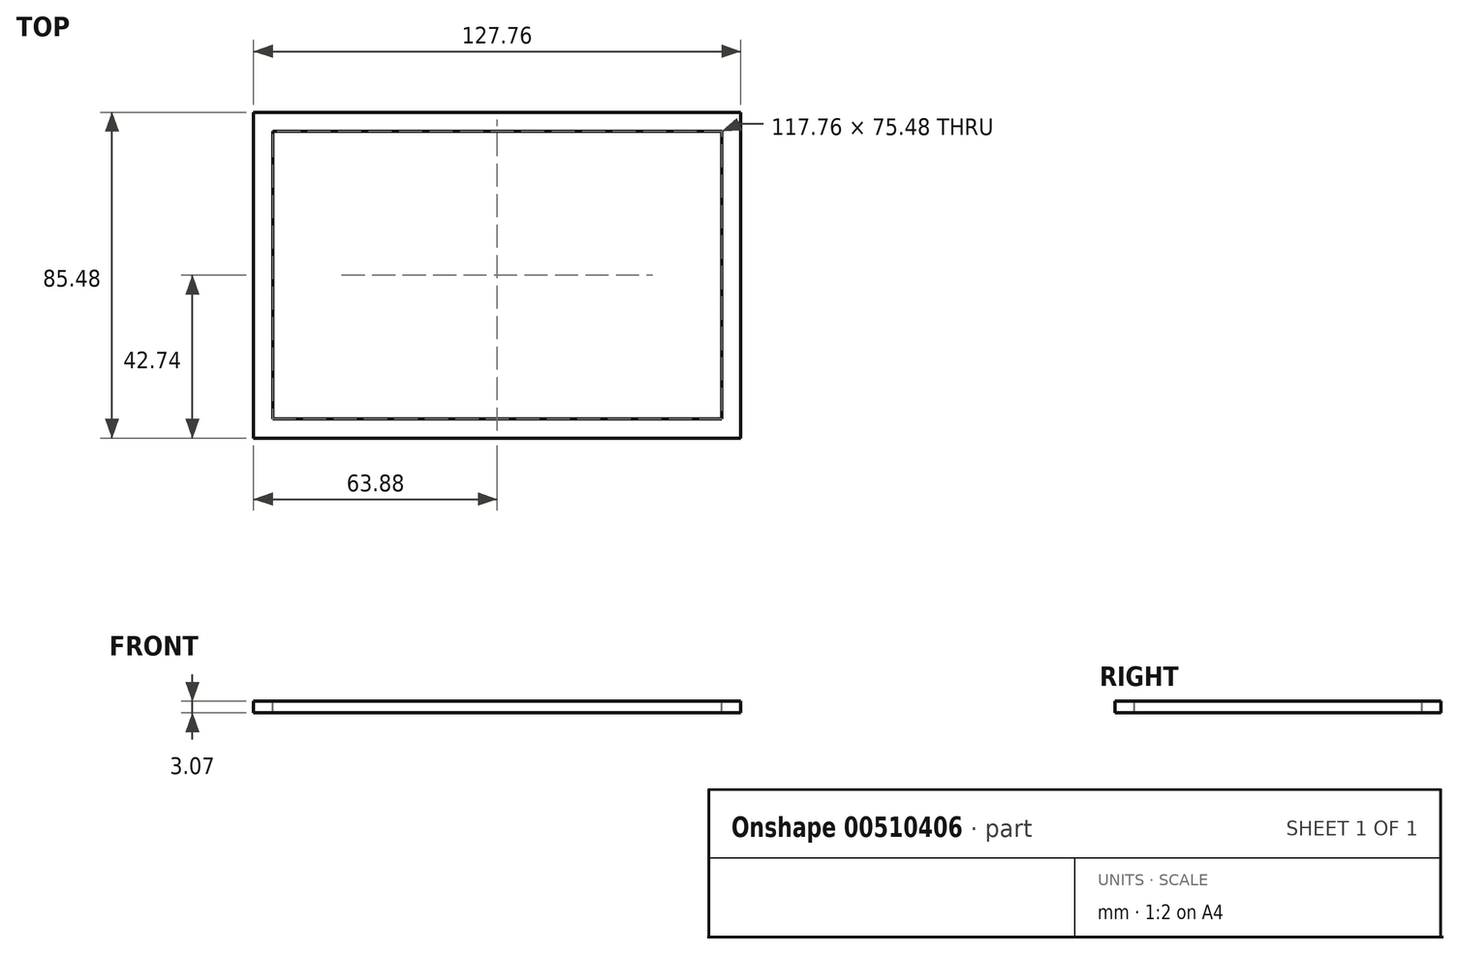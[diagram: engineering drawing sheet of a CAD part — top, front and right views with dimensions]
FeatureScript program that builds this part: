
annotation { "Feature Type Name" : "Feature", "Feature Type Description" : "" }
export const myFeature = defineFeature(function(context is Context, id is Id, definition is map)
    precondition{}
    {
        {
            var Q0;
            Q0=qCreatedBy(makeId("Top.planeOp"),FACE);
            var sketch = newSketch(context, id + "F0", { "sketchPlane" : qUnion([Q0])});
            skPoint(sketch, "E0.middle", {"position": v(0, 0) * mm});
            skLineSegment(sketch, "E1.bottom", {"start": v(63.88, -42.74) * mm, "end": v(-63.88, -42.74) * mm});
            skLineSegment(sketch, "E1.top", {"start": v(63.88, 42.74) * mm, "end": v(-63.88, 42.74) * mm});
            skLineSegment(sketch, "E1.left", {"start": v(63.88, -42.74) * mm, "end": v(63.88, 42.74) * mm});
            skLineSegment(sketch, "E1.right", {"start": v(-63.88, -42.74) * mm, "end": v(-63.88, 42.74) * mm});
            skLineSegment(sketch, "E2.bottom", {"start": v(58.88, -37.74) * mm, "end": v(-58.88, -37.74) * mm});
            skLineSegment(sketch, "E2.top", {"start": v(58.88, 37.74) * mm, "end": v(-58.88, 37.74) * mm});
            skLineSegment(sketch, "E2.left", {"start": v(58.88, -37.74) * mm, "end": v(58.88, 37.74) * mm});
            skLineSegment(sketch, "E2.right", {"start": v(-58.88, -37.74) * mm, "end": v(-58.88, 37.74) * mm});
            skSolve(sketch);
        }
        {
            var Q0;
            Q0=makeQuery(id+"F0.imprint","IMPRINT",FACE,{"disambiguationData":[TD([[makeQuery(id+"F0.imprint","IMPRINT",EDGE,{"derivedFrom":sQuery(id+"F0.wireOp",EDGE,"E1.bottom")}),-1.0]])]});
            extrude(context, id + "F1", {"entities" : qUnion([Q0]), "oppositeDirection" : true, "depth" : 3.07 * mm});
        }
    });
